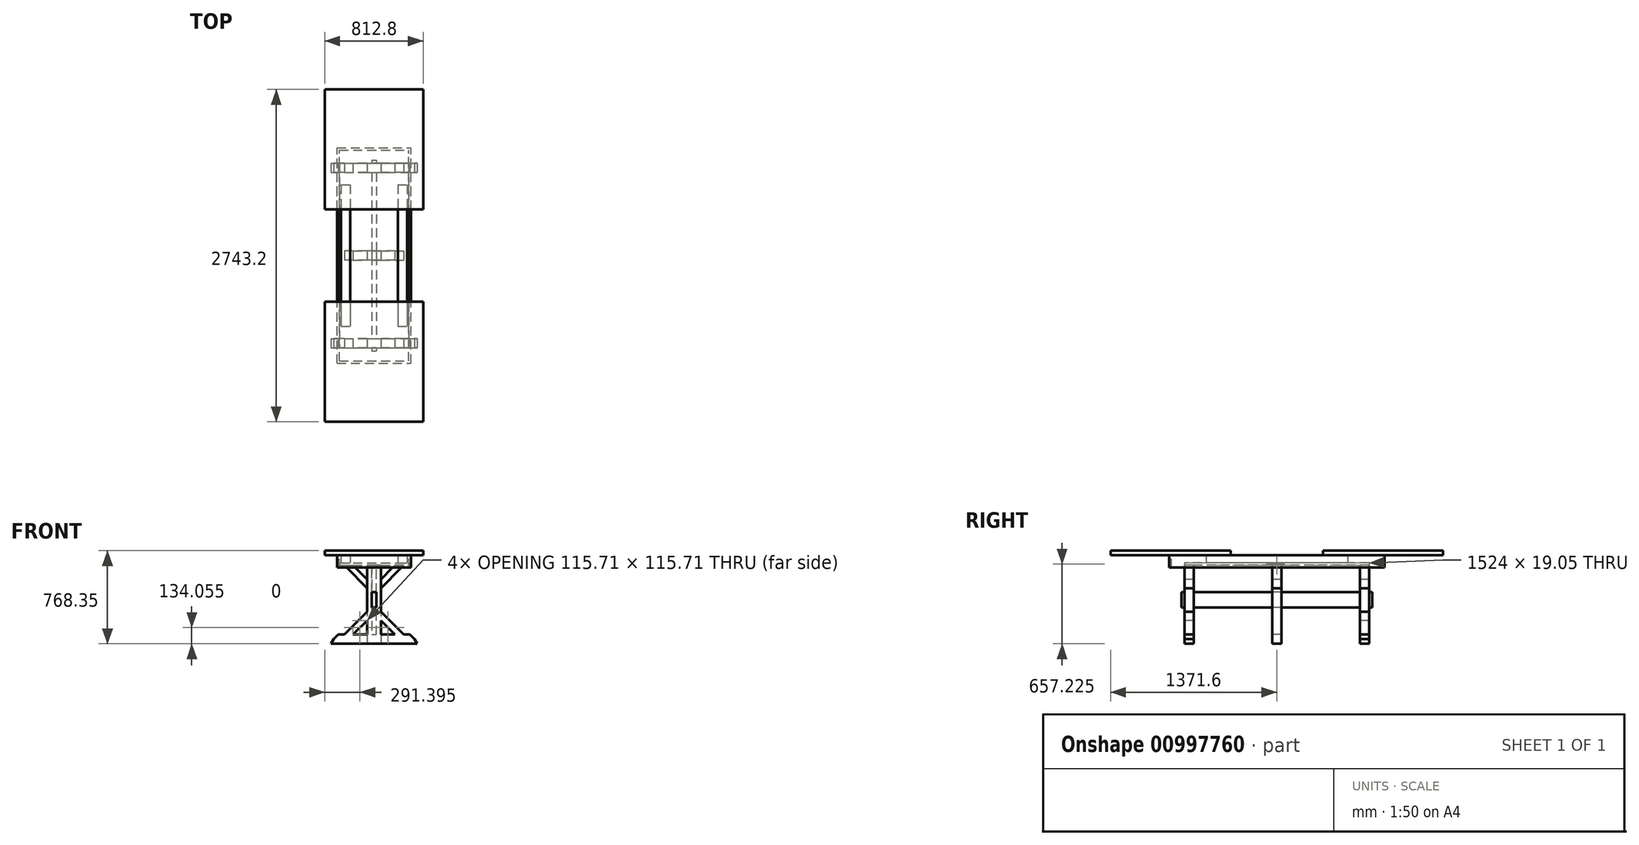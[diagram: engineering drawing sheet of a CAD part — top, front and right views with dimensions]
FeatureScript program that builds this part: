
annotation { "Feature Type Name" : "Feature", "Feature Type Description" : "" }
export const myFeature = defineFeature(function(context is Context, id is Id, definition is map)
    precondition{}
    {
        {
            var Q0;
            Q0=qCreatedBy(makeId("Front.planeOp"),FACE);
            var sketch = newSketch(context, id + "F0", { "sketchPlane" : qUnion([Q0])});
            skLineSegment(sketch, "E0", {"start": v(0, 76.2) * mm, "end": v(-295.5, 76.2) * mm});
            skLineSegment(sketch, "E1", {"start": v(-295.5, 76.2) * mm, "end": v(-333.6, 38.1) * mm});
            skLineSegment(sketch, "E2", {"start": v(0, 0) * mm, "end": v(0, 762) * mm, "construction": true});
            skLineSegment(sketch, "E3", {"start": v(-333.6, 38.1) * mm, "end": v(0, 38.1) * mm});
            skLineSegment(sketch, "E4", {"start": v(0, 76.2) * mm, "end": v(-19.05, 76.2) * mm});
            skLineSegment(sketch, "E5", {"start": v(-19.05, 76.2) * mm, "end": v(-19.05, 298.45) * mm});
            skLineSegment(sketch, "E6", {"start": v(-19.05, 298.45) * mm, "end": v(0, 298.45) * mm});
            skLineSegment(sketch, "E7", {"start": v(-19.05, 76.2) * mm, "end": v(-57.15, 76.2) * mm});
            skLineSegment(sketch, "E8", {"start": v(-57.15, 76.2) * mm, "end": v(-57.15, 647.7) * mm});
            skLineSegment(sketch, "E9", {"start": v(-57.15, 647.7) * mm, "end": v(-19.05, 647.7) * mm});
            skLineSegment(sketch, "E10", {"start": v(-19.05, 647.7) * mm, "end": v(-19.05, 76.2) * mm});
            skLineSegment(sketch, "E11", {"start": v(-355.6, 0) * mm, "end": v(0, 0) * mm});
            skLineSegment(sketch, "E12", {"start": v(0, 762) * mm, "end": v(-406.4, 762) * mm});
            skLineSegment(sketch, "E13", {"start": v(-406.4, 762) * mm, "end": v(-406.4, 723.9) * mm});
            skLineSegment(sketch, "E14", {"start": v(-406.4, 723.9) * mm, "end": v(0, 723.9) * mm});
            skLineSegment(sketch, "E15.bottom", {"start": v(-266.7, 723.9) * mm, "end": v(-200.03, 723.9) * mm, "construction": true});
            skLineSegment(sketch, "E15.top", {"start": v(-266.7, 666.75) * mm, "end": v(-200.03, 666.75) * mm, "construction": true});
            skLineSegment(sketch, "E15.left", {"start": v(-266.7, 723.9) * mm, "end": v(-266.7, 666.75) * mm, "construction": true});
            skLineSegment(sketch, "E15.right", {"start": v(-200.03, 723.9) * mm, "end": v(-200.03, 666.75) * mm, "construction": true});
            skLineSegment(sketch, "E16.bottom", {"start": v(-285.75, 666.75) * mm, "end": v(0, 666.75) * mm});
            skLineSegment(sketch, "E16.top", {"start": v(-285.75, 647.7) * mm, "end": v(0, 647.7) * mm});
            skLineSegment(sketch, "E16.left", {"start": v(-285.75, 666.75) * mm, "end": v(-285.75, 647.7) * mm});
            skLineSegment(sketch, "E17.bottom", {"start": v(-304.8, 723.9) * mm, "end": v(-285.75, 723.9) * mm});
            skLineSegment(sketch, "E17.top", {"start": v(-304.8, 622.3) * mm, "end": v(-285.75, 622.3) * mm});
            skLineSegment(sketch, "E17.left", {"start": v(-304.8, 723.9) * mm, "end": v(-304.8, 622.3) * mm});
            skLineSegment(sketch, "E17.right", {"start": v(-285.75, 723.9) * mm, "end": v(-285.75, 622.3) * mm});
            skLineSegment(sketch, "E18", {"start": v(-355.6, 0) * mm, "end": v(-333.6, 38.1) * mm});
            skLineSegment(sketch, "E19", {"start": v(-19.05, 647.7) * mm, "end": v(-19.05, 425.45) * mm});
            skLineSegment(sketch, "E20", {"start": v(-19.05, 425.45) * mm, "end": v(0, 425.45) * mm});
            skPoint(sketch, "E21", {"position": v(-19.05, 361.95) * mm});
            skLineSegment(sketch, "E22.MirrorCS", {"start": v(355.6, 0) * mm, "end": v(0, 0) * mm});
            skLineSegment(sketch, "E23.MirrorCS", {"start": v(333.6, 38.1) * mm, "end": v(0, 38.1) * mm});
            skLineSegment(sketch, "E24.MirrorCS", {"start": v(355.6, 0) * mm, "end": v(333.6, 38.1) * mm});
            skLineSegment(sketch, "E25.MirrorCS", {"start": v(295.5, 76.2) * mm, "end": v(333.6, 38.1) * mm});
            skLineSegment(sketch, "E26.MirrorCS", {"start": v(0, 76.2) * mm, "end": v(295.5, 76.2) * mm});
            skLineSegment(sketch, "E27.MirrorCS", {"start": v(57.15, 76.2) * mm, "end": v(57.15, 647.7) * mm});
            skLineSegment(sketch, "E28.MirrorCS", {"start": v(19.05, 647.7) * mm, "end": v(19.05, 76.2) * mm});
            skLineSegment(sketch, "E29.MirrorCS", {"start": v(19.05, 76.2) * mm, "end": v(57.15, 76.2) * mm});
            skLineSegment(sketch, "E30.MirrorCS", {"start": v(0, 762) * mm, "end": v(406.4, 762) * mm});
            skLineSegment(sketch, "E31.MirrorCS", {"start": v(406.4, 762) * mm, "end": v(406.4, 723.9) * mm});
            skLineSegment(sketch, "E32.MirrorCS", {"start": v(406.4, 723.9) * mm, "end": v(0, 723.9) * mm});
            skLineSegment(sketch, "E33.MirrorCS", {"start": v(285.75, 723.9) * mm, "end": v(285.75, 622.3) * mm});
            skLineSegment(sketch, "E34.MirrorCS", {"start": v(304.8, 723.9) * mm, "end": v(304.8, 622.3) * mm});
            skLineSegment(sketch, "E35.MirrorCS", {"start": v(304.8, 622.3) * mm, "end": v(285.75, 622.3) * mm});
            skLineSegment(sketch, "E36.MirrorCS", {"start": v(285.75, 647.7) * mm, "end": v(0, 647.7) * mm});
            skLineSegment(sketch, "E37.MirrorCS", {"start": v(266.7, 666.75) * mm, "end": v(200.03, 666.75) * mm, "construction": true});
            skLineSegment(sketch, "E38.MirrorCS", {"start": v(266.7, 723.9) * mm, "end": v(266.7, 666.75) * mm, "construction": true});
            skLineSegment(sketch, "E39.MirrorCS", {"start": v(200.03, 723.9) * mm, "end": v(200.03, 666.75) * mm, "construction": true});
            skLineSegment(sketch, "E40.MirrorCS", {"start": v(266.7, 723.9) * mm, "end": v(200.03, 723.9) * mm, "construction": true});
            skLineSegment(sketch, "E41.MirrorCS", {"start": v(285.75, 666.75) * mm, "end": v(0, 666.75) * mm});
            skLineSegment(sketch, "E42.MirrorCS", {"start": v(19.05, 425.45) * mm, "end": v(0, 425.45) * mm});
            skLineSegment(sketch, "E43.MirrorCS", {"start": v(19.05, 298.45) * mm, "end": v(0, 298.45) * mm});
            skLineSegment(sketch, "E44", {"start": v(57.15, 191.91) * mm, "end": v(172.86, 76.2) * mm});
            skLineSegment(sketch, "E45", {"start": v(172.86, 76.2) * mm, "end": v(244.7, 76.2) * mm});
            skLineSegment(sketch, "E46", {"start": v(244.7, 76.2) * mm, "end": v(57.15, 263.75) * mm});
            skLineSegment(sketch, "E47", {"start": v(57.15, 263.75) * mm, "end": v(57.15, 191.91) * mm});
            skLineSegment(sketch, "E48", {"start": v(-19.05, 361.95) * mm, "end": v(417.93, 361.95) * mm, "construction": true});
            skLineSegment(sketch, "E49.MirrorCS", {"start": v(244.7, 647.7) * mm, "end": v(57.15, 460.15) * mm});
            skLineSegment(sketch, "E50.MirrorCS", {"start": v(57.15, 531.99) * mm, "end": v(172.86, 647.7) * mm});
            skLineSegment(sketch, "E51.MirrorCS", {"start": v(-244.7, 76.2) * mm, "end": v(-57.15, 263.75) * mm});
            skLineSegment(sketch, "E52.MirrorCS", {"start": v(-57.15, 191.91) * mm, "end": v(-172.86, 76.2) * mm});
            skLineSegment(sketch, "E53.MirrorCS", {"start": v(-244.7, 647.7) * mm, "end": v(-57.15, 460.15) * mm});
            skLineSegment(sketch, "E54.MirrorCS", {"start": v(-57.15, 531.99) * mm, "end": v(-172.86, 647.7) * mm});
            skSolve(sketch);
        }
        {
            var Q0;
            Q0=makeQuery(id+"F0.imprint","IMPRINT",FACE,{"disambiguationData":[TD([[makeQuery(id+"F0.imprint","IMPRINT",EDGE,{"derivedFrom":sQuery(id+"F0.wireOp",EDGE,"E3")}),-1.0]])]});
            var Q1;
            {var subQ4=sQuery(id+"F0.wireOp",EDGE,"E1");Q1=makeQuery(id+"F0.imprint","IMPRINT",FACE,{"disambiguationData":[TD([[makeQuery(id+"F0.imprint","IMPRINT",EDGE,{"derivedFrom":subQ4}),1.0]])]});}
            extrude(context, id + "F1", {"entities" : qUnion([Q0, Q1]), "oppositeDirection" : true, "depth" : 76.2 * mm, "offsetDistance" : 25.4 * mm});
        }
        {
            var Q0;
            {var subQ0=sQuery(id+"F0.wireOp",EDGE,"E27.MirrorCS");var subQ4=sQuery(id+"F0.wireOp",EDGE,"E26.MirrorCS");var subQ5=makeQuery(id+"F0.imprint","INTERSECT",VERTEX,{"derivedFrom":[subQ4,subQ0]});Q0=makeQuery(id+"F0.imprint","IMPRINT",FACE,{"disambiguationData":[TD([[makeQuery(id+"F0.imprint","IMPRINT",EDGE,{"disambiguationData":[TD([[subQ5,1.0]])],"derivedFrom":subQ4}),1.0]])]});}
            var Q1;
            {var subQ6=sQuery(id+"F0.wireOp",EDGE,"E5");Q1=makeQuery(id+"F0.imprint","IMPRINT",FACE,{"disambiguationData":[TD([[makeQuery(id+"F0.imprint","IMPRINT",EDGE,{"derivedFrom":subQ6}),1.0]])]});}
            extrude(context, id + "F2", {"entities" : qUnion([Q0, Q1]), "operationType" : NewBodyOperationType.ADD, "oppositeDirection" : true, "depth" : 76.2 * mm, "offsetDistance" : 25.4 * mm});
        }
        {
            var Q0;
            {var subQ0=sQuery(id+"F0.wireOp",EDGE,"E51.MirrorCS");Q0=makeQuery(id+"F0.imprint","IMPRINT",FACE,{"disambiguationData":[TD([[makeQuery(id+"F0.imprint","IMPRINT",EDGE,{"derivedFrom":subQ0}),-1.0]])]});}
            var Q1;
            {var subQ0=sQuery(id+"F0.wireOp",EDGE,"E44");Q1=makeQuery(id+"F0.imprint","IMPRINT",FACE,{"disambiguationData":[TD([[makeQuery(id+"F0.imprint","IMPRINT",EDGE,{"derivedFrom":subQ0}),1.0]])]});}
            extrude(context, id + "F3", {"entities" : qUnion([Q0, Q1]), "operationType" : NewBodyOperationType.ADD, "oppositeDirection" : true, "depth" : 76.2 * mm, "offsetDistance" : 25.4 * mm});
        }
        {
            var Q0;
            {var subQ5=sQuery(id+"F0.wireOp",EDGE,"E5");Q0=makeQuery(id+"F0.imprint","IMPRINT",FACE,{"disambiguationData":[TD([[makeQuery(id+"F0.imprint","IMPRINT",EDGE,{"derivedFrom":subQ5}),-1.0]])]});}
            var Q1;
            {var subQ0=sQuery(id+"F0.wireOp",EDGE,"E20");Q1=makeQuery(id+"F0.imprint","IMPRINT",FACE,{"disambiguationData":[TD([[makeQuery(id+"F0.imprint","IMPRINT",EDGE,{"derivedFrom":subQ0}),1.0]])]});}
            extrude(context, id + "F4", {"entities" : qUnion([Q0, Q1]), "oppositeDirection" : true, "depth" : 76.2 * mm, "offsetDistance" : 25.4 * mm});
        }
        {
            var Q0;
            {var subQ2=sQuery(id+"F0.wireOp",EDGE,"E53.MirrorCS");Q0=makeQuery(id+"F0.imprint","IMPRINT",FACE,{"disambiguationData":[TD([[makeQuery(id+"F0.imprint","IMPRINT",EDGE,{"derivedFrom":subQ2}),1.0]])]});}
            var Q1;
            {var subQ2=sQuery(id+"F0.wireOp",EDGE,"E49.MirrorCS");Q1=makeQuery(id+"F0.imprint","IMPRINT",FACE,{"disambiguationData":[TD([[makeQuery(id+"F0.imprint","IMPRINT",EDGE,{"derivedFrom":subQ2}),-1.0]])]});}
            extrude(context, id + "F5", {"entities" : qUnion([Q0, Q1]), "oppositeDirection" : true, "depth" : 76.2 * mm, "offsetDistance" : 25.4 * mm});
        }
        {
            var Q0;
            {var subQ0=sQuery(id+"F0.wireOp",EDGE,"E27.MirrorCS");var subQ1=sQuery(id+"F0.wireOp",EDGE,"E26.MirrorCS");var subQ2=sQuery(id+"F0.wireOp",EDGE,"E8");var subQ3=sQuery(id+"F0.wireOp",EDGE,"E0");Q0=makeQuery(id+"F3.boolean.opBoolean","MERGE",FACE,{"derivedFrom":[makeQuery(id+"F2.boolean.opBoolean","MERGE",FACE,{"derivedFrom":[makeQuery(id+"F1.opExtrude","CAP_FACE",FACE,{"disambiguationData":[OSD([subQ3,sQuery(id+"F0.wireOp",EDGE,"E1"),sQuery(id+"F0.wireOp",EDGE,"E11"),sQuery(id+"F0.wireOp",EDGE,"E18"),sQuery(id+"F0.wireOp",EDGE,"E22.MirrorCS"),sQuery(id+"F0.wireOp",EDGE,"E24.MirrorCS"),sQuery(id+"F0.wireOp",EDGE,"E25.MirrorCS"),subQ1])],"isStart":false}),makeQuery(id+"F2.opExtrude","CAP_FACE",FACE,{"disambiguationData":[OSD([subQ3,sQuery(id+"F0.wireOp",EDGE,"E5"),subQ2,sQuery(id+"F0.wireOp",EDGE,"E9"),sQuery(id+"F0.wireOp",EDGE,"E10")])],"isStart":false}),makeQuery(id+"F2.opExtrude","CAP_FACE",FACE,{"disambiguationData":[OSD([subQ1,subQ0,sQuery(id+"F0.wireOp",EDGE,"E28.MirrorCS"),sQuery(id+"F0.wireOp",EDGE,"E36.MirrorCS")])],"isStart":false})]}),makeQuery(id+"F3.opExtrude","CAP_FACE",FACE,{"disambiguationData":[OSD([subQ3,subQ2,sQuery(id+"F0.wireOp",EDGE,"E51.MirrorCS"),sQuery(id+"F0.wireOp",EDGE,"E52.MirrorCS")])],"isStart":false}),makeQuery(id+"F3.opExtrude","CAP_FACE",FACE,{"disambiguationData":[OSD([subQ1,subQ0,sQuery(id+"F0.wireOp",EDGE,"E44"),sQuery(id+"F0.wireOp",EDGE,"E46")])],"isStart":false})]});}
            var Q1;
            Q1=makeQuery(id+"F5.opExtrude","CAP_FACE",FACE,{"disambiguationData":[OSD([sQuery(id+"F0.wireOp",EDGE,"E27.MirrorCS"),sQuery(id+"F0.wireOp",EDGE,"E36.MirrorCS"),sQuery(id+"F0.wireOp",EDGE,"E49.MirrorCS"),sQuery(id+"F0.wireOp",EDGE,"E50.MirrorCS")])],"isStart":false});
            var Q2;
            Q2=makeQuery(id+"F5.opExtrude","CAP_FACE",FACE,{"disambiguationData":[OSD([sQuery(id+"F0.wireOp",EDGE,"E8"),sQuery(id+"F0.wireOp",EDGE,"E16.top"),sQuery(id+"F0.wireOp",EDGE,"E53.MirrorCS"),sQuery(id+"F0.wireOp",EDGE,"E54.MirrorCS")])],"isStart":false});
            var Q3;
            Q3=makeQuery(id+"F4.opExtrude","CAP_FACE",FACE,{"disambiguationData":[OSD([sQuery(id+"F0.wireOp",EDGE,"E10"),sQuery(id+"F0.wireOp",EDGE,"E16.top"),sQuery(id+"F0.wireOp",EDGE,"E20"),sQuery(id+"F0.wireOp",EDGE,"E28.MirrorCS"),sQuery(id+"F0.wireOp",EDGE,"E36.MirrorCS"),sQuery(id+"F0.wireOp",EDGE,"E42.MirrorCS")])],"isStart":false});
            var Q4;
            Q4=makeQuery(id+"F4.opExtrude","CAP_FACE",FACE,{"disambiguationData":[OSD([sQuery(id+"F0.wireOp",EDGE,"E0"),sQuery(id+"F0.wireOp",EDGE,"E5"),sQuery(id+"F0.wireOp",EDGE,"E6"),sQuery(id+"F0.wireOp",EDGE,"E26.MirrorCS"),sQuery(id+"F0.wireOp",EDGE,"E28.MirrorCS"),sQuery(id+"F0.wireOp",EDGE,"E43.MirrorCS")])],"isStart":false});
            extrude(context, id + "F6", {"entities" : qUnion([Q0, Q1, Q2, Q3, Q4]), "depth" : 1447.8 * mm, "offsetDistance" : 25.4 * mm});
        }
        {
            var Q0;
            Q0=qCreatedBy(makeId("Right.planeOp"),FACE);
            var sketch = newSketch(context, id + "F7", { "sketchPlane" : qUnion([Q0])});
            skLineSegment(sketch, "E55.bottom", {"start": v(76.2, -1.7) * mm, "end": v(723.9, -1.7) * mm});
            skLineSegment(sketch, "E55.top", {"start": v(76.2, 696.31) * mm, "end": v(723.9, 696.31) * mm});
            skLineSegment(sketch, "E55.left", {"start": v(76.2, -1.7) * mm, "end": v(76.2, 696.31) * mm});
            skLineSegment(sketch, "E55.right", {"start": v(1447.8, -1.7) * mm, "end": v(1447.8, 696.31) * mm});
            skLineSegment(sketch, "E56.left", {"start": v(800.1, 696.31) * mm, "end": v(800.1, -1.7) * mm});
            skLineSegment(sketch, "E56.right", {"start": v(723.9, 696.31) * mm, "end": v(723.9, -1.7) * mm});
            skPoint(sketch, "E57", {"position": v(762, 696.31) * mm});
            skLineSegment(sketch, "E58.trimOffspring", {"start": v(800.1, -1.7) * mm, "end": v(1447.8, -1.7) * mm});
            skLineSegment(sketch, "E59.trimOffspring", {"start": v(800.1, 696.31) * mm, "end": v(1447.8, 696.31) * mm});
            skSolve(sketch);
        }
        {
            var Q0;
            Q0=qSketchRegion(id+"F7",true);
            extrude(context, id + "F8", {"entities" : qUnion([Q0]), "operationType" : NewBodyOperationType.REMOVE, "endBound" : BoundingType.SYMMETRIC, "oppositeDirection" : true, "depth" : 1016 * mm, "offsetDistance" : 25.4 * mm});
        }
        {
            var Q0;
            {var subQ5=sQuery(id+"F0.wireOp",EDGE,"E6");Q0=makeQuery(id+"F0.imprint","IMPRINT",FACE,{"disambiguationData":[TD([[makeQuery(id+"F0.imprint","IMPRINT",EDGE,{"derivedFrom":subQ5}),1.0]])]});}
            extrude(context, id + "F9", {"entities" : qUnion([Q0]), "oppositeDirection" : true, "depth" : 1524 * mm, "offsetDistance" : 25.4 * mm});
        }
        {
            var Q0;
            {var subQ5=sQuery(id+"F0.wireOp",EDGE,"E6");Q0=makeQuery(id+"F0.imprint","IMPRINT",FACE,{"disambiguationData":[TD([[makeQuery(id+"F0.imprint","IMPRINT",EDGE,{"derivedFrom":subQ5}),1.0]])]});}
            extrude(context, id + "F10", {"entities" : qUnion([Q0]), "operationType" : NewBodyOperationType.ADD, "depth" : 25.4 * mm, "offsetDistance" : 25.4 * mm});
        }
        {
            var Q0;
            Q0=makeQuery(id+"F9.opExtrude","CAP_FACE",FACE,{"disambiguationData":[OSD([sQuery(id+"F0.wireOp",EDGE,"E6"),sQuery(id+"F0.wireOp",EDGE,"E10"),sQuery(id+"F0.wireOp",EDGE,"E20"),sQuery(id+"F0.wireOp",EDGE,"E28.MirrorCS"),sQuery(id+"F0.wireOp",EDGE,"E42.MirrorCS"),sQuery(id+"F0.wireOp",EDGE,"E43.MirrorCS")])],"isStart":false});
            extrude(context, id + "F11", {"entities" : qUnion([Q0]), "operationType" : NewBodyOperationType.ADD, "depth" : 25.4 * mm, "offsetDistance" : 25.4 * mm});
        }
        {
            var Q0;
            {var subQ4=sQuery(id+"F0.wireOp",EDGE,"E36.MirrorCS");var subQ5=makeQuery(id+"F6.opExtrude","SWEPT_FACE",FACE,{"disambiguationData":[OSD([subQ4]),TDD([makeQuery(id+"F5.opExtrude","CAP_EDGE",EDGE,{"disambiguationData":[OSD([subQ4])],"isStart":false})])]});Q0=qUnion([makeQuery(id+"F8.boolean.opBoolean","SPLIT",FACE,{"disambiguationData":[TD([makeQuery(id+"F8.opExtrude","SWEPT_FACE",FACE,{"disambiguationData":[OSD([sQuery(id+"F7.wireOp",EDGE,"E55.right")])]})])],"derivedFrom":subQ5}),makeQuery(id+"F8.boolean.opBoolean","SPLIT",FACE,{"disambiguationData":[TD([makeQuery(id+"F8.opExtrude","SWEPT_FACE",FACE,{"disambiguationData":[OSD([sQuery(id+"F7.wireOp",EDGE,"E56.left")])]})])],"derivedFrom":subQ5})]);}
            var sketch = newSketch(context, id + "F12", { "sketchPlane" : qUnion([Q0])});
            skLineSegment(sketch, "E60.bottom", {"start": v(-285.75, 1524) * mm, "end": v(285.75, 1524) * mm});
            skLineSegment(sketch, "E60.top", {"start": v(-285.75, 0) * mm, "end": v(285.75, 0) * mm});
            skLineSegment(sketch, "E60.left", {"start": v(-285.75, 1524) * mm, "end": v(-285.75, 0) * mm});
            skLineSegment(sketch, "E60.right", {"start": v(285.75, 1524) * mm, "end": v(285.75, 0) * mm});
            skSolve(sketch);
        }
        {
            var Q0;
            Q0=qSketchRegion(id+"F12",true);
            extrude(context, id + "F13", {"entities" : qUnion([Q0]), "depth" : 19.05 * mm, "offsetDistance" : 25.4 * mm});
        }
        {
            var Q0;
            Q0=makeQuery(id+"F13.opExtrude","CAP_FACE",FACE,{"disambiguationData":[OSD([sQuery(id+"F12.wireOp",EDGE,"E60.bottom"),sQuery(id+"F12.wireOp",EDGE,"E60.top"),sQuery(id+"F12.wireOp",EDGE,"E60.left"),sQuery(id+"F12.wireOp",EDGE,"E60.right")])],"isStart":false});
            var sketch = newSketch(context, id + "F14", { "sketchPlane" : qUnion([Q0])});
            skLineSegment(sketch, "E61", {"start": v(-273.05, 762) * mm, "end": v(273.05, 762) * mm, "construction": true});
            skLineSegment(sketch, "E62.bottom", {"start": v(-273.05, 1346.2) * mm, "end": v(-196.85, 1346.2) * mm});
            skLineSegment(sketch, "E62.top", {"start": v(-273.05, 177.8) * mm, "end": v(-196.85, 177.8) * mm});
            skLineSegment(sketch, "E62.left", {"start": v(-273.05, 1346.2) * mm, "end": v(-273.05, 177.8) * mm});
            skLineSegment(sketch, "E62.right", {"start": v(-196.85, 1346.2) * mm, "end": v(-196.85, 177.8) * mm});
            skLineSegment(sketch, "E63.bottom", {"start": v(196.85, 1346.2) * mm, "end": v(273.05, 1346.2) * mm});
            skLineSegment(sketch, "E63.top", {"start": v(196.85, 177.8) * mm, "end": v(273.05, 177.8) * mm});
            skLineSegment(sketch, "E63.left", {"start": v(196.85, 1346.2) * mm, "end": v(196.85, 177.8) * mm});
            skLineSegment(sketch, "E63.right", {"start": v(273.05, 1346.2) * mm, "end": v(273.05, 177.8) * mm});
            skSolve(sketch);
        }
        {
            var Q0;
            Q0=makeQuery(id+"F14.imprint","IMPRINT",FACE,{"disambiguationData":[TD([[makeQuery(id+"F14.imprint","IMPRINT",EDGE,{"derivedFrom":sQuery(id+"F14.wireOp",EDGE,"E62.bottom")}),-1.0]])]});
            var Q1;
            Q1=makeQuery(id+"F14.imprint","IMPRINT",FACE,{"disambiguationData":[TD([[makeQuery(id+"F14.imprint","IMPRINT",EDGE,{"derivedFrom":sQuery(id+"F14.wireOp",EDGE,"E63.bottom")}),-1.0]])]});
            extrude(context, id + "F15", {"entities" : qUnion([Q0, Q1]), "operationType" : NewBodyOperationType.ADD, "depth" : 63.5 * mm, "offsetDistance" : 25.4 * mm});
        }
        {
            var Q0;
            Q0=makeQuery(id+"F15.opExtrude","CAP_FACE",FACE,{"disambiguationData":[OSD([sQuery(id+"F14.wireOp",EDGE,"E62.bottom"),sQuery(id+"F14.wireOp",EDGE,"E62.top"),sQuery(id+"F14.wireOp",EDGE,"E62.left"),sQuery(id+"F14.wireOp",EDGE,"E62.right")])],"isStart":false});
            var sketch = newSketch(context, id + "F16", { "sketchPlane" : qUnion([Q0])});
            skLineSegment(sketch, "E64.bottom", {"start": v(-406.4, 2133.6) * mm, "end": v(406.4, 2133.6) * mm});
            skLineSegment(sketch, "E64.top", {"start": v(-406.4, -609.6) * mm, "end": v(406.4, -609.6) * mm});
            skLineSegment(sketch, "E64.left", {"start": v(-406.4, 2133.6) * mm, "end": v(-406.4, 1143) * mm});
            skLineSegment(sketch, "E64.right", {"start": v(406.4, 2133.6) * mm, "end": v(406.4, 1143) * mm});
            skLineSegment(sketch, "E65", {"start": v(0, 0) * mm, "end": v(0, -609.6) * mm, "construction": true});
            skLineSegment(sketch, "E66.bottom", {"start": v(-406.4, 381) * mm, "end": v(406.4, 381) * mm});
            skLineSegment(sketch, "E66.top", {"start": v(-406.4, 1143) * mm, "end": v(406.4, 1143) * mm});
            skLineSegment(sketch, "E67.trimOffspring", {"start": v(-406.4, 381) * mm, "end": v(-406.4, -609.6) * mm});
            skLineSegment(sketch, "E68.trimOffspring", {"start": v(406.4, 381) * mm, "end": v(406.4, -609.6) * mm});
            skSolve(sketch);
        }
        {
            var Q0;
            Q0=qSketchRegion(id+"F16",true);
            extrude(context, id + "F17", {"entities" : qUnion([Q0]), "operationType" : NewBodyOperationType.ADD, "depth" : 38.1 * mm, "offsetDistance" : 25.4 * mm});
        }
        {
            var Q0;
            Q0=makeQuery(id+"F17.opExtrude","CAP_FACE",FACE,{"disambiguationData":[OSD([sQuery(id+"F16.wireOp",EDGE,"E64.bottom"),sQuery(id+"F16.wireOp",EDGE,"E64.top"),sQuery(id+"F16.wireOp",EDGE,"E64.left"),sQuery(id+"F16.wireOp",EDGE,"E64.right")])],"isStart":true});
            var sketch = newSketch(context, id + "F18", { "sketchPlane" : qUnion([Q0])});
            skLineSegment(sketch, "E69.bottom", {"start": v(-304.8, 127) * mm, "end": v(304.8, 127) * mm});
            skLineSegment(sketch, "E69.top", {"start": v(-304.8, -1651) * mm, "end": v(304.8, -1651) * mm});
            skLineSegment(sketch, "E69.left", {"start": v(-304.8, 127) * mm, "end": v(-304.8, -1651) * mm});
            skLineSegment(sketch, "E69.right", {"start": v(304.8, 127) * mm, "end": v(304.8, -1651) * mm});
            skLineSegment(sketch, "E70.bottom", {"start": v(-285.75, 107.95) * mm, "end": v(285.75, 107.95) * mm});
            skLineSegment(sketch, "E70.top", {"start": v(-285.75, -1631.95) * mm, "end": v(273.05, -1631.95) * mm});
            skLineSegment(sketch, "E70.left", {"start": v(-285.75, 107.95) * mm, "end": v(-285.75, -1631.95) * mm});
            skLineSegment(sketch, "E70.right", {"start": v(285.75, 107.95) * mm, "end": v(285.75, -1631.95) * mm});
            skLineSegment(sketch, "E71", {"start": v(273.05, -1631.95) * mm, "end": v(285.75, -1631.95) * mm});
            skSolve(sketch);
        }
        {
            var Q0;
            {var subQ13=sQuery(id+"F18.wireOp",EDGE,"E69.bottom");Q0=makeQuery(id+"F18.imprint","IMPRINT",FACE,{"disambiguationData":[TD([[makeQuery(id+"F18.imprint","IMPRINT",EDGE,{"derivedFrom":subQ13}),-1.0]])]});}
            var Q1;
            {var subQ2=sQuery(id+"F18.wireOp",EDGE,"E69.top");Q1=makeQuery(id+"F18.imprint","IMPRINT",FACE,{"disambiguationData":[TD([[makeQuery(id+"F18.imprint","IMPRINT",EDGE,{"derivedFrom":subQ2}),1.0]])]});}
            extrude(context, id + "F19", {"entities" : qUnion([Q0, Q1]), "operationType" : NewBodyOperationType.ADD, "depth" : 101.6 * mm, "offsetDistance" : 25.4 * mm});
        }
        {
            var Q0;
            {var subQ13=sQuery(id+"F0.wireOp",EDGE,"E1");Q0=makeQuery(id+"F8.boolean.opBoolean","COPY",FACE,{"disambiguationData":[TD([makeQuery(id+"F6.opExtrude","SWEPT_FACE",FACE,{"disambiguationData":[OSD([subQ13])]})])],"derivedFrom":makeQuery(id+"F8.opExtrude","SWEPT_FACE",FACE,{"disambiguationData":[OSD([sQuery(id+"F7.wireOp",EDGE,"E56.left")])]})});}
            var sketch = newSketch(context, id + "F20", { "sketchPlane" : qUnion([Q0])});
            skLineSegment(sketch, "E72.bottom", {"start": v(57.15, 263.75) * mm, "end": v(510, 263.75) * mm});
            skLineSegment(sketch, "E72.top", {"start": v(57.15, -83.18) * mm, "end": v(510, -83.18) * mm});
            skLineSegment(sketch, "E72.left", {"start": v(57.15, 263.75) * mm, "end": v(57.15, -83.18) * mm});
            skLineSegment(sketch, "E72.right", {"start": v(510, 263.75) * mm, "end": v(510, -83.18) * mm});
            skLineSegment(sketch, "E73.bottom", {"start": v(-57.15, 263.75) * mm, "end": v(-399.16, 263.75) * mm});
            skLineSegment(sketch, "E73.top", {"start": v(-57.15, -37.53) * mm, "end": v(-399.16, -37.53) * mm});
            skLineSegment(sketch, "E73.left", {"start": v(-57.15, 263.75) * mm, "end": v(-57.15, -37.53) * mm});
            skLineSegment(sketch, "E73.right", {"start": v(-399.16, 263.75) * mm, "end": v(-399.16, -37.53) * mm});
            skSolve(sketch);
        }
        {
            var Q0;
            Q0=qSketchRegion(id+"F20",true);
            extrude(context, id + "F21", {"entities" : qUnion([Q0]), "operationType" : NewBodyOperationType.REMOVE, "oppositeDirection" : true, "depth" : 101.6 * mm, "offsetDistance" : 25.4 * mm});
        }
    });
